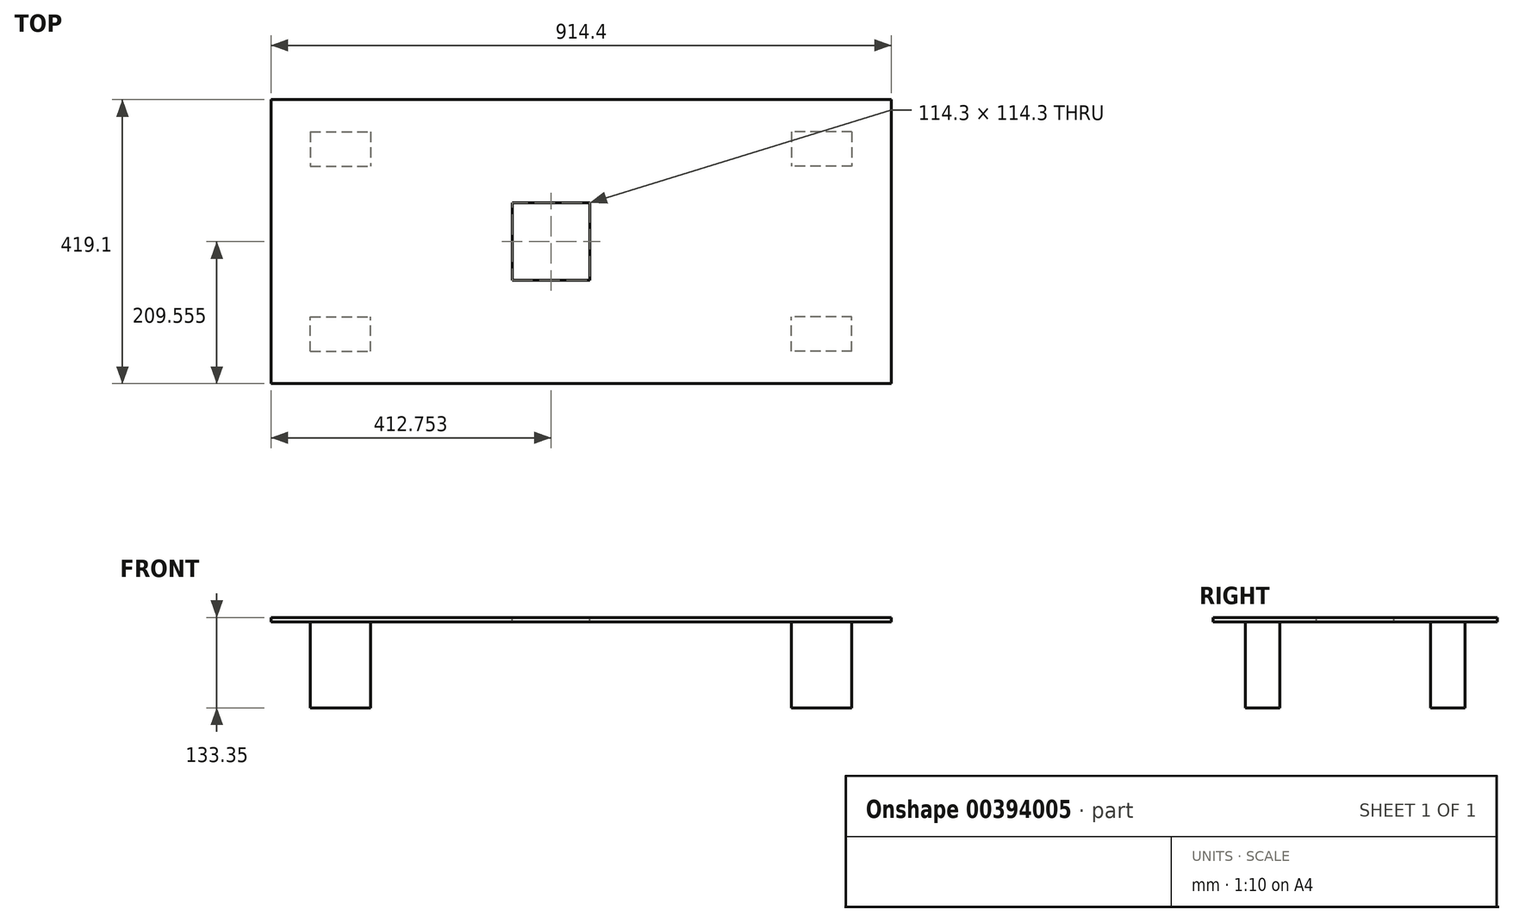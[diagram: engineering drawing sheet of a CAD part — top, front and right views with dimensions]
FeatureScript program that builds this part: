
annotation { "Feature Type Name" : "Feature", "Feature Type Description" : "" }
export const myFeature = defineFeature(function(context is Context, id is Id, definition is map)
    precondition{}
    {
        {
            var Q0;
            Q0=qCreatedBy(makeId("Top.planeOp"),FACE);
            var sketch = newSketch(context, id + "F0", { "sketchPlane" : qUnion([Q0])});
            skLineSegment(sketch, "E0.bottom", {"start": v(-449.1, 46.96) * mm, "end": v(465.3, 46.96) * mm});
            skLineSegment(sketch, "E0.top", {"start": v(-449.1, -372.14) * mm, "end": v(465.3, -372.14) * mm});
            skLineSegment(sketch, "E0.left", {"start": v(-449.1, 46.96) * mm, "end": v(-449.1, -372.14) * mm});
            skLineSegment(sketch, "E0.right", {"start": v(465.3, 46.96) * mm, "end": v(465.3, -372.14) * mm});
            skSolve(sketch);
        }
        {
            var Q0;
            Q0=qSketchRegion(id+"F0",true);
            extrude(context, id + "F1", {"entities" : qUnion([Q0]), "depth" : 6.35 * mm});
        }
        {
            var Q0;
            Q0=makeQuery(id+"F1.opExtrude","CAP_FACE",FACE,{"disambiguationData":[OSD([sQuery(id+"F0.wireOp",EDGE,"E0.bottom"),sQuery(id+"F0.wireOp",EDGE,"E0.top"),sQuery(id+"F0.wireOp",EDGE,"E0.left"),sQuery(id+"F0.wireOp",EDGE,"E0.right")])],"isStart":true});
            var sketch = newSketch(context, id + "F2", { "sketchPlane" : qUnion([Q0])});
            skLineSegment(sketch, "E1.bottom", {"start": v(-390.97, 324.5) * mm, "end": v(-302.07, 324.5) * mm});
            skLineSegment(sketch, "E1.top", {"start": v(-390.97, 273.7) * mm, "end": v(-302.07, 273.7) * mm});
            skLineSegment(sketch, "E1.left", {"start": v(-390.97, 324.5) * mm, "end": v(-390.97, 273.7) * mm});
            skLineSegment(sketch, "E1.right", {"start": v(-302.07, 324.5) * mm, "end": v(-302.07, 273.7) * mm});
            skLineSegment(sketch, "E2", {"start": v(8.1, 372.14) * mm, "end": v(8.1, -46.96) * mm, "construction": true});
            skLineSegment(sketch, "E3", {"start": v(-449.1, 162.59) * mm, "end": v(465.3, 162.59) * mm, "construction": true});
            skLineSegment(sketch, "E4.MirrorCS", {"start": v(-390.97, 0.66) * mm, "end": v(-302.07, 0.66) * mm});
            skLineSegment(sketch, "E5.MirrorCS", {"start": v(-302.07, 0.66) * mm, "end": v(-302.07, 51.46) * mm});
            skLineSegment(sketch, "E6.MirrorCS", {"start": v(-390.97, 51.46) * mm, "end": v(-302.07, 51.46) * mm});
            skLineSegment(sketch, "E7.MirrorCS", {"start": v(-390.97, 0.66) * mm, "end": v(-390.97, 51.46) * mm});
            skLineSegment(sketch, "E8.MirrorCS", {"start": v(407.15, 324.5) * mm, "end": v(407.15, 273.7) * mm});
            skLineSegment(sketch, "E9.MirrorCS", {"start": v(407.15, 273.7) * mm, "end": v(318.25, 273.7) * mm});
            skLineSegment(sketch, "E10.MirrorCS", {"start": v(318.25, 324.5) * mm, "end": v(318.25, 273.7) * mm});
            skLineSegment(sketch, "E11.MirrorCS", {"start": v(407.15, 324.5) * mm, "end": v(318.25, 324.5) * mm});
            skLineSegment(sketch, "E12.MirrorCS", {"start": v(407.15, 51.46) * mm, "end": v(318.25, 51.46) * mm});
            skLineSegment(sketch, "E13.MirrorCS", {"start": v(318.25, 0.66) * mm, "end": v(318.25, 51.46) * mm});
            skLineSegment(sketch, "E14.MirrorCS", {"start": v(407.15, 0.66) * mm, "end": v(318.25, 0.66) * mm});
            skLineSegment(sketch, "E15.MirrorCS", {"start": v(407.15, 0.66) * mm, "end": v(407.15, 51.46) * mm});
            skLineSegment(sketch, "E16", {"start": v(-390.97, 324.5) * mm, "end": v(-449.1, 324.5) * mm, "construction": true});
            skLineSegment(sketch, "E17", {"start": v(-390.97, 324.5) * mm, "end": v(-390.97, 372.14) * mm, "construction": true});
            skSolve(sketch);
        }
        {
            var Q0;
            Q0=qSketchRegion(id+"F2",true);
            extrude(context, id + "F3", {"entities" : qUnion([Q0]), "operationType" : NewBodyOperationType.ADD, "depth" : 127 * mm});
        }
        {
            var Q0;
            Q0=makeQuery(id+"F1.opExtrude","CAP_FACE",FACE,{"disambiguationData":[OSD([sQuery(id+"F0.wireOp",EDGE,"E0.bottom"),sQuery(id+"F0.wireOp",EDGE,"E0.top"),sQuery(id+"F0.wireOp",EDGE,"E0.left"),sQuery(id+"F0.wireOp",EDGE,"E0.right")])],"isStart":false});
            var sketch = newSketch(context, id + "F4", { "sketchPlane" : qUnion([Q0])});
            skLineSegment(sketch, "E18.0", {"start": v(-93.5, 46.96) * mm, "end": v(-93.5, -372.14) * mm, "construction": true});
            skLineSegment(sketch, "E19.0", {"start": v(-449.1, -219.74) * mm, "end": v(363.7, -219.74) * mm, "construction": true});
            skLineSegment(sketch, "E20.bottom", {"start": v(-93.5, -219.74) * mm, "end": v(20.8, -219.74) * mm});
            skLineSegment(sketch, "E20.top", {"start": v(-93.5, -105.44) * mm, "end": v(20.8, -105.44) * mm});
            skLineSegment(sketch, "E20.left", {"start": v(-93.5, -219.74) * mm, "end": v(-93.5, -105.44) * mm});
            skLineSegment(sketch, "E20.right", {"start": v(20.8, -219.74) * mm, "end": v(20.8, -105.44) * mm});
            skSolve(sketch);
        }
        {
            var Q0;
            Q0=qSketchRegion(id+"F4",true);
            extrude(context, id + "F5", {"entities" : qUnion([Q0]), "operationType" : NewBodyOperationType.REMOVE, "oppositeDirection" : true, "depth" : 6.35 * mm});
        }
    });
